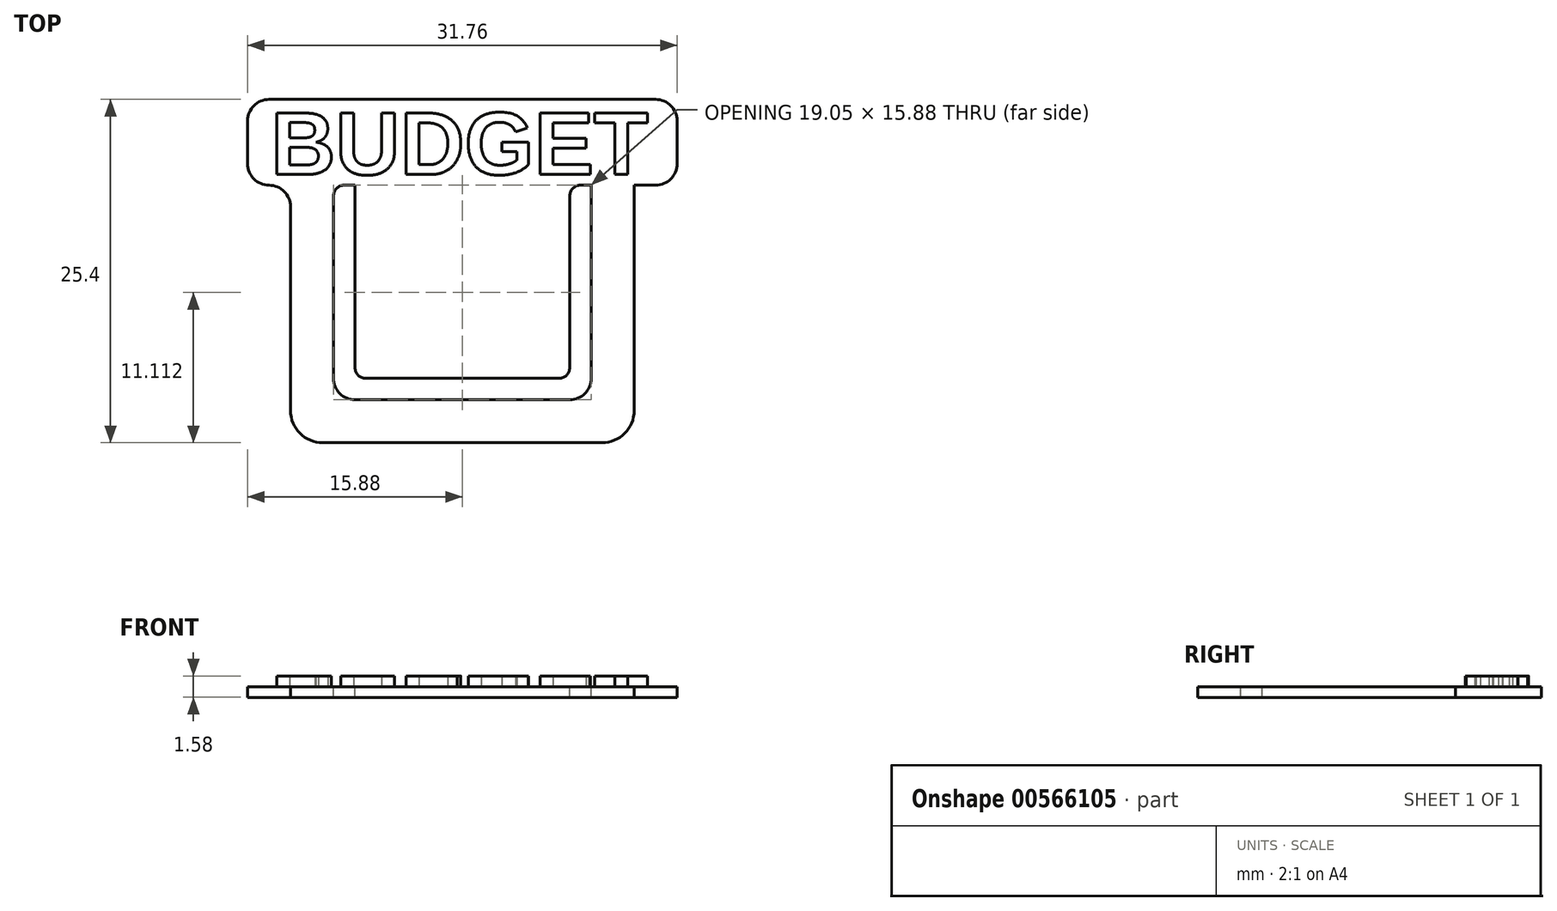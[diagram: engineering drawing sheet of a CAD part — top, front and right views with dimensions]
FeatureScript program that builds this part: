
annotation { "Feature Type Name" : "Feature", "Feature Type Description" : "" }
export const myFeature = defineFeature(function(context is Context, id is Id, definition is map)
    precondition{}
    {
        {
            var Q0;
            Q0=qCreatedBy(makeId("Front.planeOp"),FACE);
            var sketch = newSketch(context, id + "F0", { "sketchPlane" : qUnion([Q0])});
            skLineSegment(sketch, "E0.bottom", {"start": v(12.7, 9.53) * mm, "end": v(-12.7, 9.53) * mm});
            skLineSegment(sketch, "E0.top", {"start": v(12.7, -9.53) * mm, "end": v(-12.7, -9.53) * mm});
            skLineSegment(sketch, "E0.left", {"start": v(12.7, 9.53) * mm, "end": v(12.7, -9.53) * mm});
            skLineSegment(sketch, "E0.right", {"start": v(-12.7, 9.53) * mm, "end": v(-12.7, -9.53) * mm});
            skPoint(sketch, "E0.middle", {"position": v(0, 0) * mm});
            skSolve(sketch);
        }
        {
            var Q0;
            Q0=makeQuery(id+"F0.imprint","IMPRINT",FACE,{"disambiguationData":[TD([[makeQuery(id+"F0.imprint","IMPRINT",EDGE,{"derivedFrom":sQuery(id+"F0.wireOp",EDGE,"E0.bottom")}),1.0]])]});
            extrude(context, id + "F1", {"entities" : qUnion([Q0]), "depth" : 0.8 * mm, "offsetDistance" : 25.4 * mm});
        }
        {
            var Q0;
            Q0=makeQuery(id+"F1.opExtrude","SWEPT_EDGE",EDGE,{"disambiguationData":[OSD([sQuery(id+"F0.wireOp",EDGE,"E0.top"),sQuery(id+"F0.wireOp",EDGE,"E0.left")])]});
            var Q1;
            Q1=makeQuery(id+"F1.opExtrude","SWEPT_EDGE",EDGE,{"disambiguationData":[OSD([sQuery(id+"F0.wireOp",EDGE,"E0.top"),sQuery(id+"F0.wireOp",EDGE,"E0.right")])]});
            fillet(context, id + "F2", {"entities" : qUnion([Q0, Q1]), "radius" : 2.38 * mm, "tangentPropagation" : true, "allowEdgeOverflow" : false});
        }
        {
            var Q0;
            Q0=makeQuery(id+"F1.opExtrude","CAP_FACE",FACE,{"disambiguationData":[OSD([sQuery(id+"F0.wireOp",EDGE,"E0.bottom"),sQuery(id+"F0.wireOp",EDGE,"E0.top"),sQuery(id+"F0.wireOp",EDGE,"E0.left"),sQuery(id+"F0.wireOp",EDGE,"E0.right")])],"isStart":false});
            var sketch = newSketch(context, id + "F3", { "sketchPlane" : qUnion([Q0])});
            skLineSegment(sketch, "E1.bottom", {"start": v(9.52, 9.53) * mm, "end": v(-9.53, 9.53) * mm});
            skLineSegment(sketch, "E1.top", {"start": v(9.53, -6.35) * mm, "end": v(-9.53, -6.35) * mm});
            skLineSegment(sketch, "E1.left", {"start": v(9.52, 9.53) * mm, "end": v(9.53, -6.35) * mm});
            skLineSegment(sketch, "E1.right", {"start": v(-9.53, 9.53) * mm, "end": v(-9.52, -6.35) * mm});
            skPoint(sketch, "E1.middle", {"position": v(0, 0) * mm});
            skSolve(sketch);
        }
        {
            var Q0;
            Q0=makeQuery(id+"F3.imprint","IMPRINT",FACE,{"disambiguationData":[TD([[makeQuery(id+"F3.imprint","IMPRINT",EDGE,{"derivedFrom":sQuery(id+"F3.wireOp",EDGE,"E1.bottom")}),1.0]])]});
            extrude(context, id + "F4", {"entities" : qUnion([Q0]), "operationType" : NewBodyOperationType.REMOVE, "oppositeDirection" : true, "depth" : 4.93 * mm, "offsetDistance" : 25.4 * mm});
        }
        {
            var Q0;
            Q0=makeQuery(id+"F1.opExtrude","CAP_FACE",FACE,{"disambiguationData":[OSD([sQuery(id+"F0.wireOp",EDGE,"E0.bottom"),sQuery(id+"F0.wireOp",EDGE,"E0.top"),sQuery(id+"F0.wireOp",EDGE,"E0.left"),sQuery(id+"F0.wireOp",EDGE,"E0.right")])],"isStart":false});
            var sketch = newSketch(context, id + "F5", { "sketchPlane" : qUnion([Q0])});
            skLineSegment(sketch, "E2.bottom", {"start": v(-15.88, 9.53) * mm, "end": v(15.87, 9.53) * mm});
            skLineSegment(sketch, "E2.top", {"start": v(-15.88, 15.88) * mm, "end": v(15.87, 15.88) * mm});
            skLineSegment(sketch, "E2.left", {"start": v(-15.88, 9.53) * mm, "end": v(-15.88, 15.88) * mm});
            skLineSegment(sketch, "E2.right", {"start": v(15.87, 9.53) * mm, "end": v(15.87, 15.88) * mm});
            skSolve(sketch);
        }
        {
            var Q0;
            Q0=makeQuery(id+"F5.imprint","IMPRINT",FACE,{"disambiguationData":[TD([[makeQuery(id+"F5.imprint","IMPRINT",EDGE,{"derivedFrom":sQuery(id+"F5.wireOp",EDGE,"E2.top")}),-1.0]])]});
            extrude(context, id + "F6", {"entities" : qUnion([Q0]), "operationType" : NewBodyOperationType.ADD, "oppositeDirection" : true, "depth" : 0.8 * mm, "offsetDistance" : 25.4 * mm});
        }
        {
            var Q0;
            Q0=makeQuery(id+"F6.opExtrude","SWEPT_EDGE",EDGE,{"disambiguationData":[OSD([sQuery(id+"F5.wireOp",EDGE,"E2.top"),sQuery(id+"F5.wireOp",EDGE,"E2.left")])]});
            var Q1;
            Q1=makeQuery(id+"F6.opExtrude","SWEPT_EDGE",EDGE,{"disambiguationData":[OSD([sQuery(id+"F5.wireOp",EDGE,"E2.top"),sQuery(id+"F5.wireOp",EDGE,"E2.right")])]});
            var Q2;
            Q2=makeQuery(id+"F6.opExtrude","SWEPT_EDGE",EDGE,{"disambiguationData":[OSD([sQuery(id+"F5.wireOp",EDGE,"E2.bottom"),sQuery(id+"F5.wireOp",EDGE,"E2.right")])]});
            var Q3;
            Q3=makeQuery(id+"F1.opExtrude","SWEPT_EDGE",EDGE,{"disambiguationData":[OSD([sQuery(id+"F0.wireOp",EDGE,"E0.bottom"),sQuery(id+"F0.wireOp",EDGE,"E0.left")])]});
            var Q4;
            Q4=makeQuery(id+"F6.opExtrude","SWEPT_EDGE",EDGE,{"disambiguationData":[OSD([sQuery(id+"F5.wireOp",EDGE,"E2.bottom"),sQuery(id+"F5.wireOp",EDGE,"E2.left")])]});
            var Q5;
            Q5=makeQuery(id+"F1.opExtrude","SWEPT_EDGE",EDGE,{"disambiguationData":[OSD([sQuery(id+"F0.wireOp",EDGE,"E0.bottom"),sQuery(id+"F0.wireOp",EDGE,"E0.right")])]});
            fillet(context, id + "F7", {"entities" : qUnion([Q0, Q1, Q2, Q3, Q4, Q5]), "radius" : 1.59 * mm, "tangentPropagation" : true, "allowEdgeOverflow" : false});
        }
        {
            var Q0;
            Q0=makeQuery(id+"F4.boolean.opBoolean","COPY",EDGE,{"derivedFrom":makeQuery(id+"F4.opExtrude","SWEPT_EDGE",EDGE,{"disambiguationData":[OSD([sQuery(id+"F3.wireOp",EDGE,"E1.top"),sQuery(id+"F3.wireOp",EDGE,"E1.right")])]})});
            var Q1;
            Q1=makeQuery(id+"F4.boolean.opBoolean","COPY",EDGE,{"derivedFrom":makeQuery(id+"F4.opExtrude","SWEPT_EDGE",EDGE,{"disambiguationData":[OSD([sQuery(id+"F3.wireOp",EDGE,"E1.top"),sQuery(id+"F3.wireOp",EDGE,"E1.left")])]})});
            fillet(context, id + "F8", {"entities" : qUnion([Q0, Q1]), "radius" : 1.59 * mm, "tangentPropagation" : true, "allowEdgeOverflow" : false});
        }
        {
            var Q0;
            Q0=makeQuery(id+"F6.boolean.opBoolean","MERGE",FACE,{"derivedFrom":[makeQuery(id+"F1.opExtrude","CAP_FACE",FACE,{"disambiguationData":[OSD([sQuery(id+"F0.wireOp",EDGE,"E0.bottom"),sQuery(id+"F0.wireOp",EDGE,"E0.top"),sQuery(id+"F0.wireOp",EDGE,"E0.left"),sQuery(id+"F0.wireOp",EDGE,"E0.right")])],"isStart":false}),makeQuery(id+"F6.opExtrude","CAP_FACE",FACE,{"disambiguationData":[OSD([sQuery(id+"F5.wireOp",EDGE,"E2.bottom"),sQuery(id+"F5.wireOp",EDGE,"E2.top"),sQuery(id+"F5.wireOp",EDGE,"E2.left"),sQuery(id+"F5.wireOp",EDGE,"E2.right")])],"isStart":true})]});
            var sketch = newSketch(context, id + "F9", { "sketchPlane" : qUnion([Q0])});
            skLineSegment(sketch, "E3.bottom", {"start": v(-7.94, 9.53) * mm, "end": v(7.94, 9.53) * mm});
            skLineSegment(sketch, "E3.top", {"start": v(-7.94, -4.76) * mm, "end": v(7.94, -4.76) * mm});
            skLineSegment(sketch, "E3.left", {"start": v(-7.94, 9.53) * mm, "end": v(-7.94, -4.76) * mm});
            skLineSegment(sketch, "E3.right", {"start": v(7.94, 9.53) * mm, "end": v(7.94, -4.76) * mm});
            skSolve(sketch);
        }
        {
            var Q0;
            Q0=makeQuery(id+"F9.imprint","IMPRINT",FACE,{"disambiguationData":[TD([[makeQuery(id+"F9.imprint","IMPRINT",EDGE,{"derivedFrom":sQuery(id+"F9.wireOp",EDGE,"E3.bottom")}),1.0]])]});
            extrude(context, id + "F10", {"entities" : qUnion([Q0]), "operationType" : NewBodyOperationType.ADD, "oppositeDirection" : true, "depth" : 0.8 * mm, "offsetDistance" : 25.4 * mm});
        }
        {
            var Q0;
            Q0=makeQuery(id+"F10.boolean.opBoolean","MERGE",FACE,{"derivedFrom":[makeQuery(id+"F6.boolean.opBoolean","MERGE",FACE,{"derivedFrom":[makeQuery(id+"F1.opExtrude","CAP_FACE",FACE,{"disambiguationData":[OSD([sQuery(id+"F0.wireOp",EDGE,"E0.bottom"),sQuery(id+"F0.wireOp",EDGE,"E0.top"),sQuery(id+"F0.wireOp",EDGE,"E0.left"),sQuery(id+"F0.wireOp",EDGE,"E0.right")])],"isStart":false}),makeQuery(id+"F6.opExtrude","CAP_FACE",FACE,{"disambiguationData":[OSD([sQuery(id+"F5.wireOp",EDGE,"E2.bottom"),sQuery(id+"F5.wireOp",EDGE,"E2.top"),sQuery(id+"F5.wireOp",EDGE,"E2.left"),sQuery(id+"F5.wireOp",EDGE,"E2.right")])],"isStart":true})]}),makeQuery(id+"F10.opExtrude","CAP_FACE",FACE,{"disambiguationData":[OSD([sQuery(id+"F9.wireOp",EDGE,"E3.bottom"),sQuery(id+"F9.wireOp",EDGE,"E3.top"),sQuery(id+"F9.wireOp",EDGE,"E3.left"),sQuery(id+"F9.wireOp",EDGE,"E3.right")])],"isStart":true})]});
            var sketch = newSketch(context, id + "F11", { "sketchPlane" : qUnion([Q0])});
            skText(sketch, "E4", { "text": "BUDGET", "fontName": "Arimo-Bold.ttf"});
            const initialGuessF11  = {"E4": [-0.01416, 0.01032, 1, 0, 0.00476]};
            skSetInitialGuess(sketch, initialGuessF11);
            skSolve(sketch);
        }
        {
            var Q0;
            Q0=makeQuery(id+"F11.imprint","IMPRINT",FACE,{"disambiguationData":[TD([[makeQuery(id+"F11.imprint","IMPRINT",EDGE,{"derivedFrom":sQuery(id+"F11.wireOp",EDGE,"E4.sketch_text.stroke-0")}),-1.0]])]});
            var Q1;
            Q1=makeQuery(id+"F11.imprint","IMPRINT",FACE,{"disambiguationData":[TD([[makeQuery(id+"F11.imprint","IMPRINT",EDGE,{"derivedFrom":sQuery(id+"F11.wireOp",EDGE,"E4.sketch_text.stroke-8")}),-1.0]])]});
            var Q2;
            Q2=makeQuery(id+"F11.imprint","IMPRINT",FACE,{"disambiguationData":[TD([[makeQuery(id+"F11.imprint","IMPRINT",EDGE,{"derivedFrom":sQuery(id+"F11.wireOp",EDGE,"E4.sketch_text.stroke-25")}),-1.0]])]});
            var Q3;
            Q3=makeQuery(id+"F11.imprint","IMPRINT",FACE,{"disambiguationData":[TD([[makeQuery(id+"F11.imprint","IMPRINT",EDGE,{"derivedFrom":sQuery(id+"F11.wireOp",EDGE,"E4.sketch_text.stroke-40")}),-1.0]])]});
            var Q4;
            Q4=makeQuery(id+"F11.imprint","IMPRINT",FACE,{"disambiguationData":[TD([[makeQuery(id+"F11.imprint","IMPRINT",EDGE,{"derivedFrom":sQuery(id+"F11.wireOp",EDGE,"E4.sketch_text.stroke-55")}),-1.0]])]});
            var Q5;
            Q5=makeQuery(id+"F11.imprint","IMPRINT",FACE,{"disambiguationData":[TD([[makeQuery(id+"F11.imprint","IMPRINT",EDGE,{"derivedFrom":sQuery(id+"F11.wireOp",EDGE,"E4.sketch_text.stroke-74")}),-1.0]])]});
            var Q6;
            Q6=makeQuery(id+"F11.imprint","IMPRINT",FACE,{"disambiguationData":[TD([[makeQuery(id+"F11.imprint","IMPRINT",EDGE,{"derivedFrom":sQuery(id+"F11.wireOp",EDGE,"E4.sketch_text.stroke-86")}),-1.0]])]});
            extrude(context, id + "F12", {"entities" : qUnion([Q0, Q1, Q2, Q3, Q4, Q5, Q6]), "operationType" : NewBodyOperationType.ADD, "depth" : 0.8 * mm, "offsetDistance" : 25.4 * mm});
        }
        {
            var Q0;
            Q0=makeQuery(id+"F10.opExtrude","SWEPT_EDGE",EDGE,{"disambiguationData":[OSD([sQuery(id+"F5.wireOp",EDGE,"E2.bottom"),sQuery(id+"F9.wireOp",EDGE,"E3.bottom"),sQuery(id+"F9.wireOp",EDGE,"E3.left")])]});
            var Q1;
            Q1=makeQuery(id+"F4.boolean.opBoolean","COPY",EDGE,{"derivedFrom":makeQuery(id+"F4.opExtrude","SWEPT_EDGE",EDGE,{"disambiguationData":[OSD([sQuery(id+"F0.wireOp",EDGE,"E0.bottom"),sQuery(id+"F3.wireOp",EDGE,"E1.bottom"),sQuery(id+"F3.wireOp",EDGE,"E1.right")])]})});
            var Q2;
            Q2=makeQuery(id+"F10.opExtrude","SWEPT_EDGE",EDGE,{"disambiguationData":[OSD([sQuery(id+"F5.wireOp",EDGE,"E2.bottom"),sQuery(id+"F9.wireOp",EDGE,"E3.bottom"),sQuery(id+"F9.wireOp",EDGE,"E3.right")])]});
            var Q3;
            Q3=makeQuery(id+"F4.boolean.opBoolean","COPY",EDGE,{"derivedFrom":makeQuery(id+"F4.opExtrude","SWEPT_EDGE",EDGE,{"disambiguationData":[OSD([sQuery(id+"F0.wireOp",EDGE,"E0.bottom"),sQuery(id+"F3.wireOp",EDGE,"E1.bottom"),sQuery(id+"F3.wireOp",EDGE,"E1.left")])]})});
            fillet(context, id + "F13", {"entities" : qUnion([Q0, Q1, Q2, Q3]), "radius" : 0.8 * mm, "tangentPropagation" : true, "allowEdgeOverflow" : false});
        }
        {
            var Q0;
            Q0=makeQuery(id+"F10.opExtrude","SWEPT_EDGE",EDGE,{"disambiguationData":[OSD([sQuery(id+"F9.wireOp",EDGE,"E3.top"),sQuery(id+"F9.wireOp",EDGE,"E3.left")])]});
            var Q1;
            Q1=makeQuery(id+"F10.opExtrude","SWEPT_EDGE",EDGE,{"disambiguationData":[OSD([sQuery(id+"F9.wireOp",EDGE,"E3.top"),sQuery(id+"F9.wireOp",EDGE,"E3.right")])]});
            fillet(context, id + "F14", {"entities" : qUnion([Q0, Q1]), "radius" : 0.8 * mm, "tangentPropagation" : true, "allowEdgeOverflow" : false});
        }
        {
            var Q0;
            Q0=makeQuery(id+"F1.opExtrude","SWEPT_BODY",BODY,{"disambiguationData":[OSD([sQuery(id+"F0.wireOp",EDGE,"E0.bottom"),sQuery(id+"F0.wireOp",EDGE,"E0.top"),sQuery(id+"F0.wireOp",EDGE,"E0.left"),sQuery(id+"F0.wireOp",EDGE,"E0.right")])]});
            var Q1;
            Q1=makeQuery(id+"F6.opExtrude","CAP_EDGE",EDGE,{"disambiguationData":[OSD([sQuery(id+"F5.wireOp",EDGE,"E2.top")])],"isStart":false});
            transform(context, id + "F15", {"entities" : qUnion([Q0]), "transformType" : TransformType.ROTATION, "transformAxis" : qUnion([Q1]), "angle" : 270 * degree, "makeCopy" : false});
        }
    });
